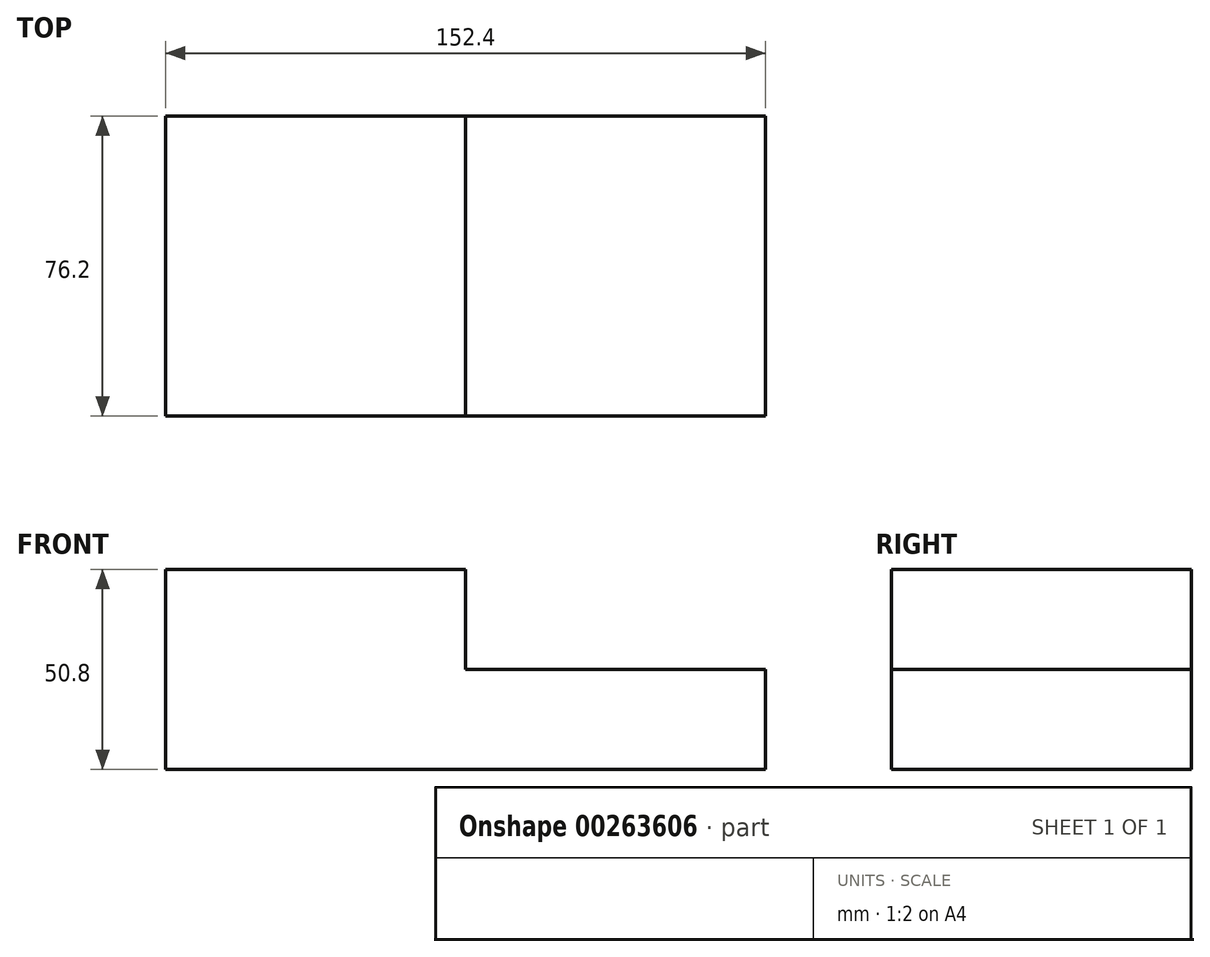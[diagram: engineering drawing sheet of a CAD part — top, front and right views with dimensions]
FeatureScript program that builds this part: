
annotation { "Feature Type Name" : "Feature", "Feature Type Description" : "" }
export const myFeature = defineFeature(function(context is Context, id is Id, definition is map)
    precondition{}
    {
        {
            var Q0;
            Q0=qCreatedBy(makeId("Front.planeOp"),FACE);
            var sketch = newSketch(context, id + "F0", { "sketchPlane" : qUnion([Q0])});
            skLineSegment(sketch, "E0", {"start": v(-76.2, 11.34) * mm, "end": v(-76.2, -39.46) * mm});
            skLineSegment(sketch, "E1", {"start": v(-76.2, -39.46) * mm, "end": v(76.2, -39.46) * mm});
            skLineSegment(sketch, "E2", {"start": v(76.2, -39.46) * mm, "end": v(76.2, -14.06) * mm});
            skLineSegment(sketch, "E3", {"start": v(76.2, -14.06) * mm, "end": v(0, -14.06) * mm});
            skLineSegment(sketch, "E4", {"start": v(0, -14.06) * mm, "end": v(0, 11.34) * mm});
            skLineSegment(sketch, "E5", {"start": v(0, 11.34) * mm, "end": v(-76.2, 11.34) * mm});
            skSolve(sketch);
        }
        {
            var Q0;
            Q0=makeQuery(id+"F0.imprint","IMPRINT",FACE,{"disambiguationData":[TD([[makeQuery(id+"F0.imprint","IMPRINT",EDGE,{"derivedFrom":sQuery(id+"F0.wireOp",EDGE,"E0")}),1.0]])]});
            extrude(context, id + "F1", {"entities" : qUnion([Q0]), "depth" : 76.2 * mm});
        }
    });
